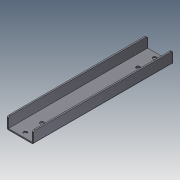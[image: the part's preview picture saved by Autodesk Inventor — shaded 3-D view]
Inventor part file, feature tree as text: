
AUTODESK INVENTOR PART (.ipt)
format: ipt  version: 2015 (Build 190159000, 159)  size: 185,344 bytes
history: native  units: mm
features: other x6, sheet_metal_op x5, sketch x4, plane x2, mirror x1, chamfer x1
ambient origin geometry x8: Origin, YZ Plane, XZ Plane, XY Plane, X Axis, Y Axis, Z Axis, Center Point
bodies: Solid1 (feature_tree)
feature tree (19):
  sheet_metal_op  "Face1"
  sheet_metal_op  "Flange1"
  sheet_metal_op  "Flange2"
  plane  "Work Plane1"
  mirror  "Mirror1"
  chamfer  "Corner Round1"
  plane  "Work Plane2"
  sketch  "Sketch1"  dims[d2=72.0mm]
  other  "Plate1"
  sketch  "Sketch2"  dims[d3=420.0mm]
  other  "Plate2"
  sheet_metal_op  "Bend1"
  sketch  "Sketch3"  dims[d4=0.001mm]
  other  "Plate3"
  sheet_metal_op  "Bend2"
  sketch  "Sketch4"  dims[d5=4.0mm d6=0.001mm d7=8.0mm d8=0.001mm d9=31.0mm d10=90.0deg d11=0.001mm d12=4.0mm d13=0.001mm d14=8.0mm d15=0.001mm d16=31.0mm d17=90.0deg d18=0.001mm d19=11.0mm d20=11.0mm d21=15.0mm d22=50.0mm d23=4.0mm d24=0.0mm d25=5.0mm d0=4.0mm]
  other  "FlatPattern"
  other  "Cut1"
  other  "FlatPatternExtrusion2"
